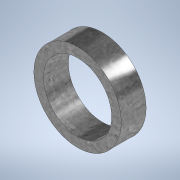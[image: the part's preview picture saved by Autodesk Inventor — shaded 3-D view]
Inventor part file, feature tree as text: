
AUTODESK INVENTOR PART (.ipt)
format: ipt  version: 2020 (Build 240168000, 168)  size: 111,104 bytes
history: native  units: in
note: dims shown in document units (in); Inventor stores cm internally (conversion verified against a paired STEP export)
features: extrude x1, sketch x1
ambient origin geometry x8: Origin, YZ Plane, XZ Plane, XY Plane, X Axis, Y Axis, Z Axis, Center Point
bodies: Solid1 (feature_tree)
feature tree (2):
  extrude  "Extrusion1"  Depth=1.0in
  sketch  "Sketch1"  dims[d0=3.51in d1=2.74in d2=1.0in d3=0.0in]
